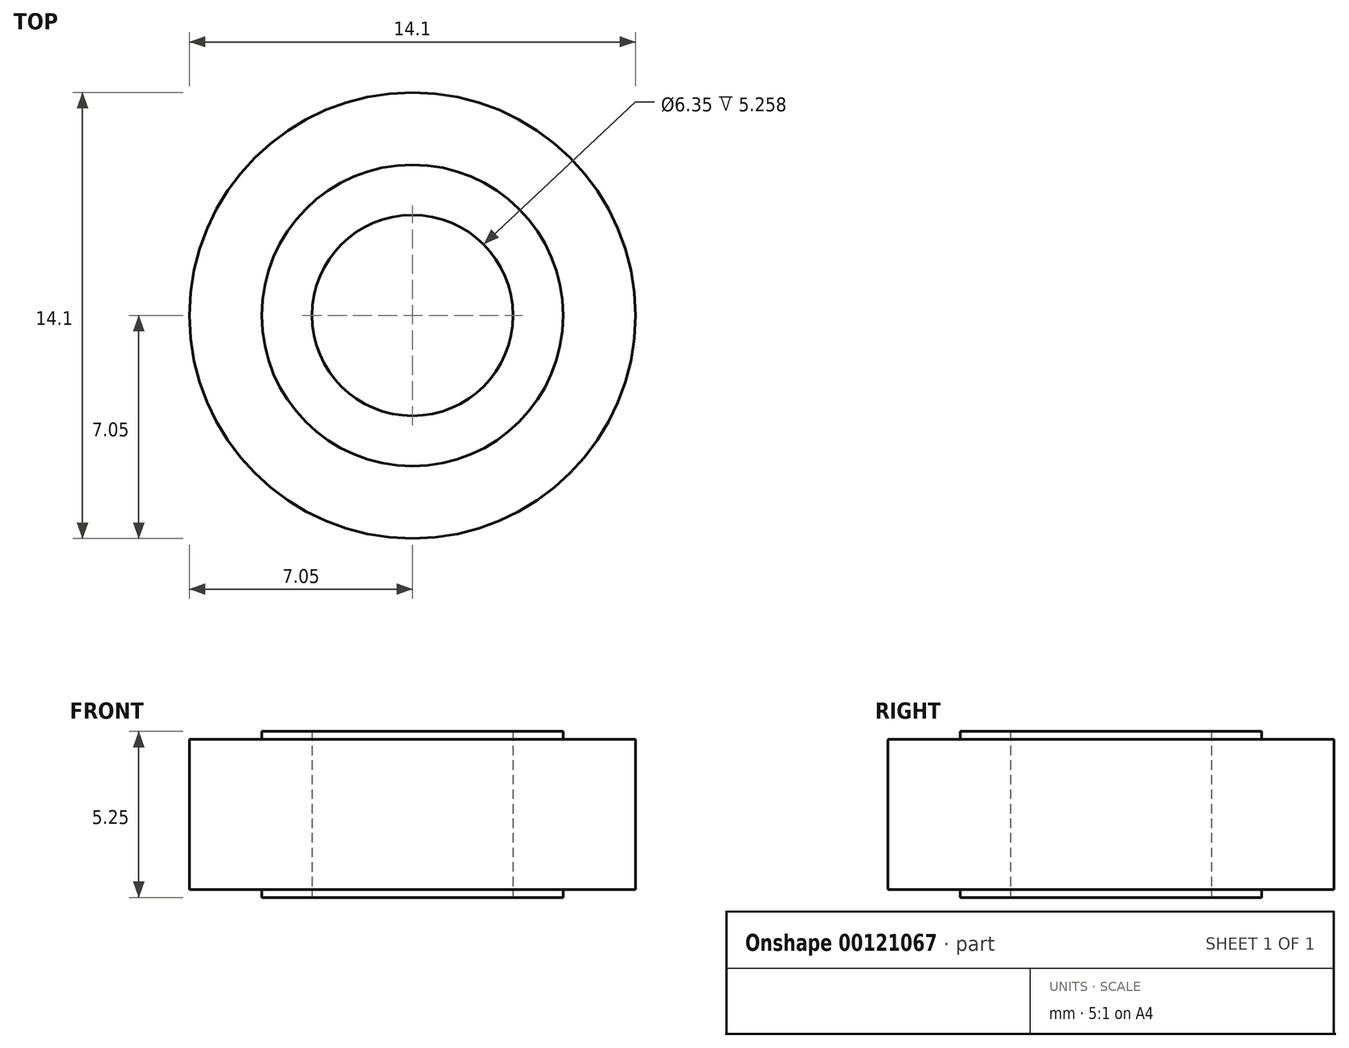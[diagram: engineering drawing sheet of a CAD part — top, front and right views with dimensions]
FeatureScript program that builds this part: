
annotation { "Feature Type Name" : "Feature", "Feature Type Description" : "" }
export const myFeature = defineFeature(function(context is Context, id is Id, definition is map)
    precondition{}
    {
        {
            var Q0;
            Q0=qCreatedBy(makeId("Top.planeOp"),FACE);
            var sketch = newSketch(context, id + "F0", { "sketchPlane" : qUnion([Q0])});
            skCircle(sketch, "E0", {"center": v(0, 0) * mm, "radius": 7.05 * mm});
            skSolve(sketch);
        }
        {
            var Q0;
            Q0 = qSketchRegion(id + "F0", true);
            extrude(context, id + "F1", {"entities" : qUnion([Q0]), "depth" : 4.75 * mm});
        }
        {
            var Q0;
            Q0=makeQuery(id+"F1.opExtrude","CAP_FACE",FACE,{"disambiguationData":[OSD([sQuery(id+"F0.wireOp",EDGE,"E0")])],"isStart":false});
            var sketch = newSketch(context, id + "F2", { "sketchPlane" : qUnion([Q0])});
            skCircle(sketch, "E1", {"center": v(0, 0) * mm, "radius": 4.76 * mm});
            skSolve(sketch);
        }
        {
            var Q0;
            Q0=makeQuery(id+"F2.imprint","IMPRINT",FACE,{"disambiguationData":[TD([[makeQuery(id+"F2.imprint","IMPRINT",EDGE,{"derivedFrom":sQuery(id+"F2.wireOp",EDGE,"E1")}),1.0]])]});
            extrude(context, id + "F3", {"entities" : qUnion([Q0]), "operationType" : NewBodyOperationType.ADD, "depth" : 0.25 * mm});
        }
        {
            var Q0;
            Q0=makeQuery(id+"F1.opExtrude","CAP_FACE",FACE,{"disambiguationData":[OSD([sQuery(id+"F0.wireOp",EDGE,"E0")])],"isStart":true});
            var sketch = newSketch(context, id + "F4", { "sketchPlane" : qUnion([Q0])});
            skCircle(sketch, "E2", {"center": v(0, 0) * mm, "radius": 4.76 * mm});
            skSolve(sketch);
        }
        {
            var Q0;
            Q0 = qSketchRegion(id + "F4", true);
            extrude(context, id + "F5", {"entities" : qUnion([Q0]), "operationType" : NewBodyOperationType.ADD, "depth" : 0.25 * mm});
        }
        {
            var Q0;
            Q0=makeQuery(id+"F5.opExtrude","CAP_FACE",FACE,{"disambiguationData":[OSD([sQuery(id+"F4.wireOp",EDGE,"E2")])],"isStart":false});
            var sketch = newSketch(context, id + "F6", { "sketchPlane" : qUnion([Q0])});
            skCircle(sketch, "E3", {"center": v(0, 0) * mm, "radius": 3.18 * mm});
            skSolve(sketch);
        }
        {
            var Q0;
            Q0 = qSketchRegion(id + "F6", true);
            extrude(context, id + "F7", {"entities" : qUnion([Q0]), "operationType" : NewBodyOperationType.REMOVE, "endBound" : BoundingType.THROUGH_ALL, "oppositeDirection" : true, "depth" : 25.4 * mm});
        }
    });
